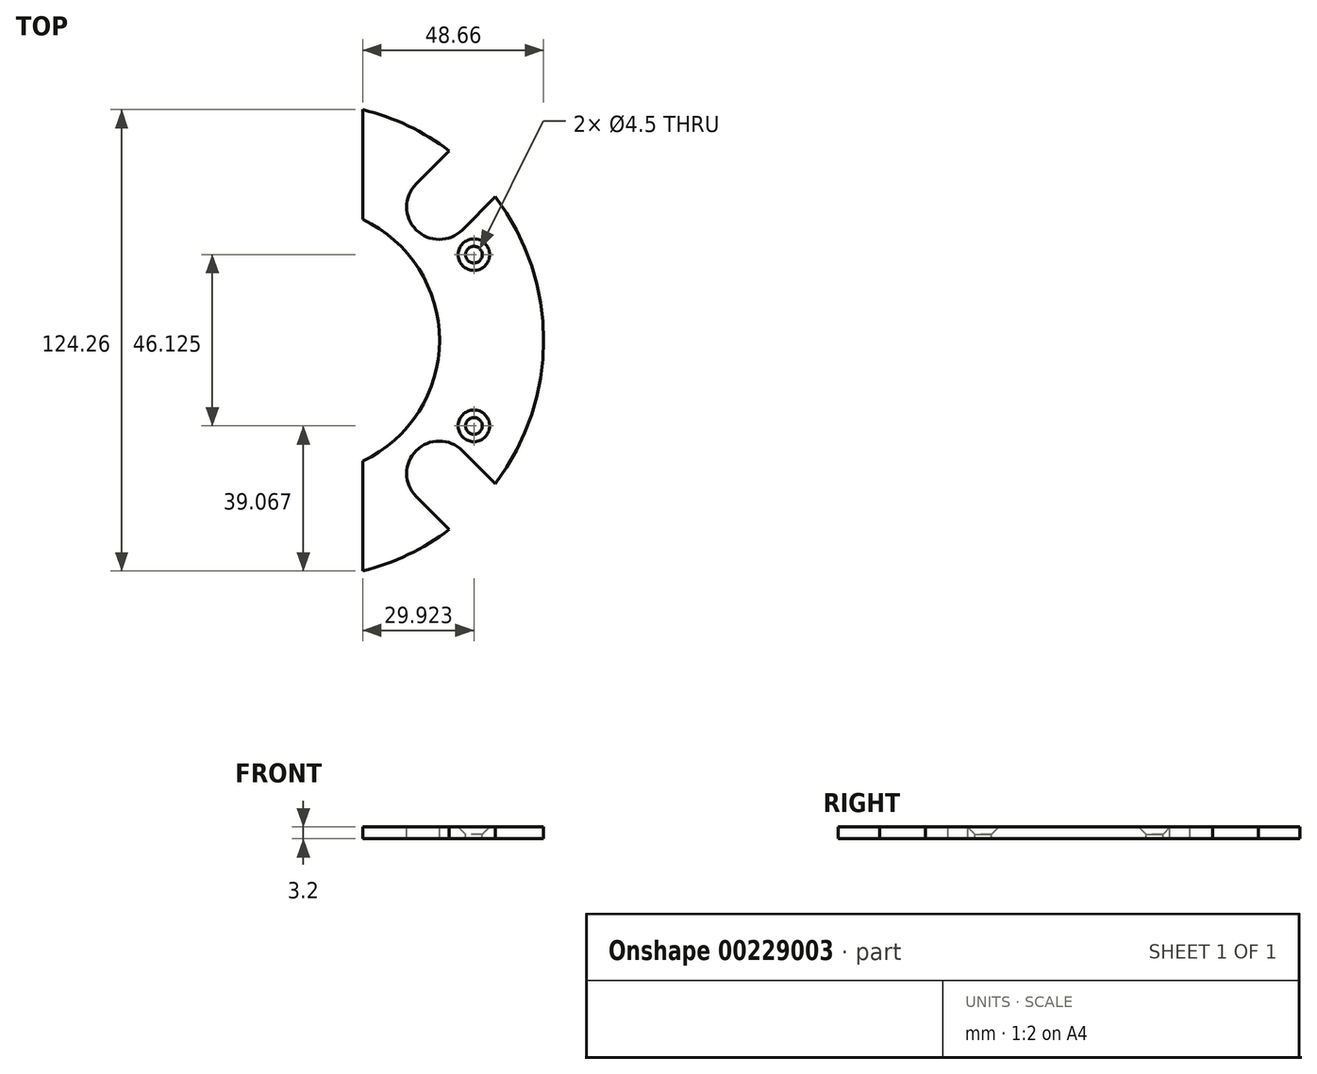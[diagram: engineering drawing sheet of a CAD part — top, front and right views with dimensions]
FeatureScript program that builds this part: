
annotation { "Feature Type Name" : "Feature", "Feature Type Description" : "" }
export const myFeature = defineFeature(function(context is Context, id is Id, definition is map)
    precondition{}
    {
        {
            var Q0;
            Q0=qCreatedBy(makeId("Top.planeOp"),FACE);
            var sketch = newSketch(context, id + "F0", { "sketchPlane" : qUnion([Q0])});
            skArc(sketch, "E0", {"start": v(15.34, -32.57) * mm, "mid": v(36, 0) * mm, "end": v(15.34, 32.57) * mm});
            skArc(sketch, "E1", {"start": v(15.34, -62.13) * mm, "mid": v(27.56, -57.76) * mm, "end": v(38.64, -51.02) * mm});
            skCircle(sketch, "E2", {"center": v(0, 0) * mm, "radius": 50.8 * mm, "construction": true});
            skLineSegment(sketch, "E3", {"start": v(0, 0) * mm, "end": v(35.92, 35.92) * mm, "construction": true});
            skLineSegment(sketch, "E4", {"start": v(0, 0) * mm, "end": v(35.92, -35.92) * mm, "construction": true});
            skLineSegment(sketch, "E5", {"start": v(15.34, 62.13) * mm, "end": v(15.34, 32.57) * mm});
            skLineSegment(sketch, "E6.trimOffspring", {"start": v(15.34, -32.57) * mm, "end": v(15.34, -62.13) * mm});
            skArc(sketch, "E7", {"start": v(29.73, 42.1) * mm, "mid": v(29.73, 29.73) * mm, "end": v(42.1, 29.73) * mm});
            skArc(sketch, "E8", {"start": v(42.1, -29.73) * mm, "mid": v(29.73, -29.73) * mm, "end": v(29.73, -42.1) * mm});
            skLineSegment(sketch, "E9", {"start": v(29.2, 41.57) * mm, "end": v(38.64, 51.02) * mm});
            skLineSegment(sketch, "E10", {"start": v(41.57, 29.2) * mm, "end": v(51.02, 38.64) * mm});
            skArc(sketch, "E11.trimOffspring", {"start": v(38.64, 51.02) * mm, "mid": v(27.56, 57.76) * mm, "end": v(15.34, 62.13) * mm});
            skLineSegment(sketch, "E12", {"start": v(41.57, -29.2) * mm, "end": v(51.02, -38.64) * mm});
            skLineSegment(sketch, "E13", {"start": v(29.2, -41.57) * mm, "end": v(38.64, -51.02) * mm});
            skArc(sketch, "E14.trimOffspring", {"start": v(51.02, -38.64) * mm, "mid": v(64, 0) * mm, "end": v(51.02, 38.64) * mm});
            skSolve(sketch);
        }
        {
            var Q0;
            Q0 = qSketchRegion(id + "F0", true);
            extrude(context, id + "F1", {"entities" : qUnion([Q0]), "oppositeDirection" : true, "depth" : 3.2 * mm});
        }
        {
            var Q0;
            Q0=makeQuery(id+"F1.opExtrude","CAP_FACE",FACE,{"disambiguationData":[OSD([sQuery(id+"F0.wireOp",EDGE,"E0"),sQuery(id+"F0.wireOp",EDGE,"E1"),sQuery(id+"F0.wireOp",EDGE,"E5"),sQuery(id+"F0.wireOp",EDGE,"E6.trimOffspring"),sQuery(id+"F0.wireOp",EDGE,"E7"),sQuery(id+"F0.wireOp",EDGE,"E8")])],"isStart":true});
            var sketch = newSketch(context, id + "F2", { "sketchPlane" : qUnion([Q0])});
            skCircle(sketch, "E15", {"center": v(0, 0) * mm, "radius": 50.8 * mm, "construction": true});
            skLineSegment(sketch, "E16", {"start": v(0, 0) * mm, "end": v(45.26, 23.06) * mm, "construction": true});
            skLineSegment(sketch, "E17", {"start": v(0, 0) * mm, "end": v(45.26, -23.06) * mm, "construction": true});
            skCircle(sketch, "E18", {"center": v(45.26, 23.06) * mm, "radius": 4.25 * mm, "construction": true});
            skPoint(sketch, "E19", {"position": v(45.26, -23.06) * mm});
            skSolve(sketch);
        }
        {
            var Q0;
            Q0=sQuery(id+"F2.wireOp",VERTEX,"E18.center");
            var Q1;
            Q1=sQuery(id+"F2.wireOp",VERTEX,"E19");
            var Q2;
            Q2=makeQuery(id+"F1.opExtrude","SWEPT_BODY",BODY,{"disambiguationData":[OSD([sQuery(id+"F0.wireOp",EDGE,"E0"),sQuery(id+"F0.wireOp",EDGE,"E1"),sQuery(id+"F0.wireOp",EDGE,"E5"),sQuery(id+"F0.wireOp",EDGE,"E6.trimOffspring"),sQuery(id+"F0.wireOp",EDGE,"E7"),sQuery(id+"F0.wireOp",EDGE,"E8")])]});
            hole(context, id + "F3", {"style" : HoleStyle.C_SINK, "endStyle" : HoleEndStyle.THROUGH, "holeDiameter" : 4.5 * mm, "cSinkDiameter" : 8.5 * mm, "cSinkAngle" : 90 * degree, "locations" : qUnion([Q0, Q1]), "scope" : qUnion([Q2]), "isTappedThrough" : true});
        }
    });
